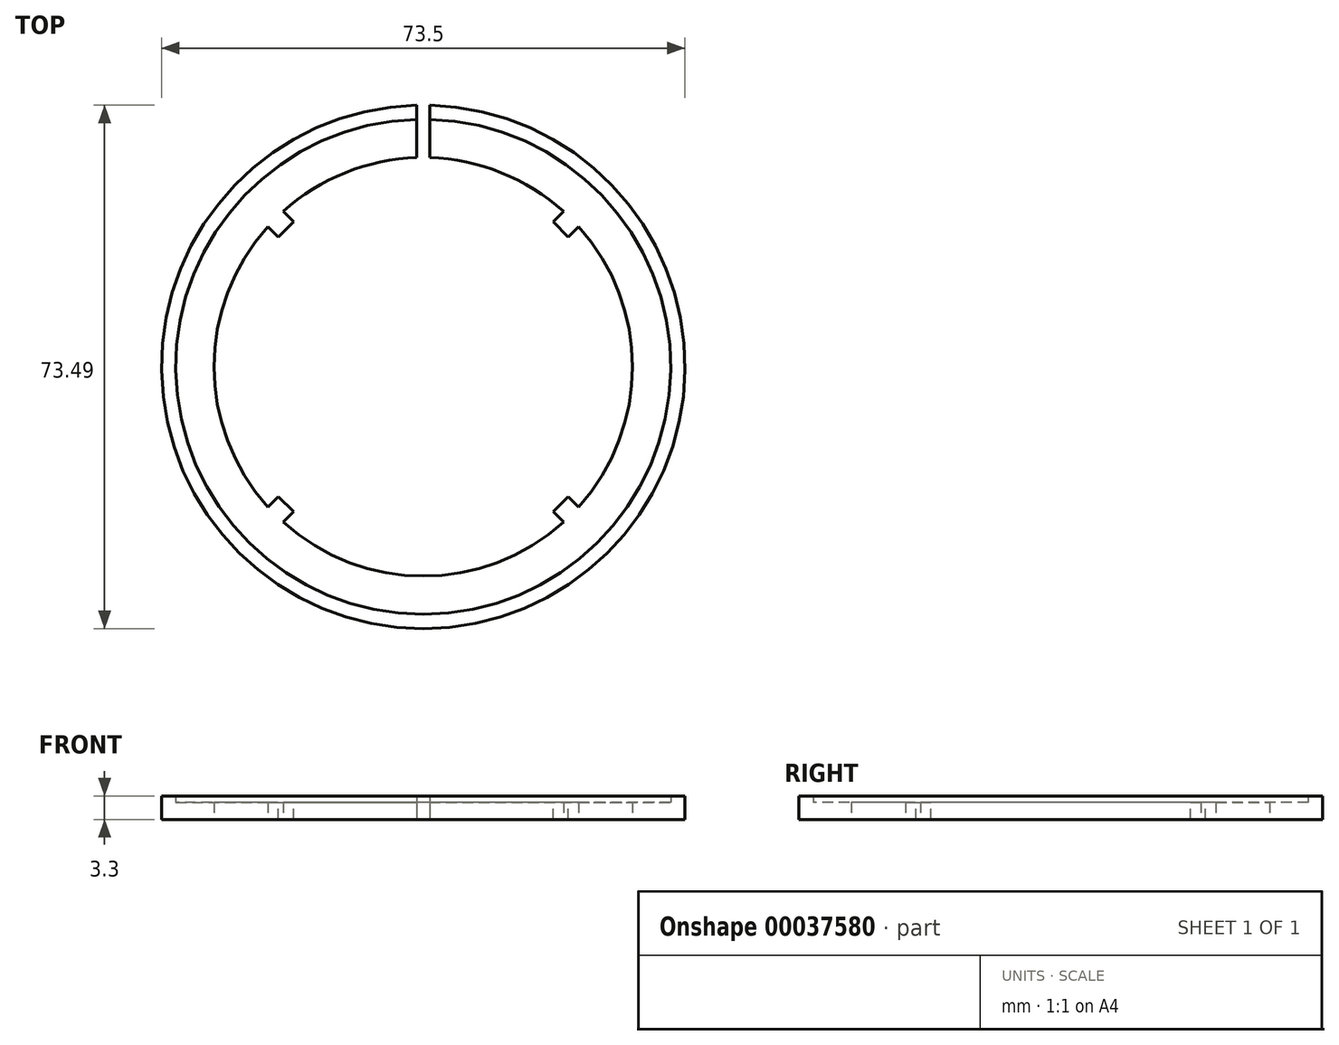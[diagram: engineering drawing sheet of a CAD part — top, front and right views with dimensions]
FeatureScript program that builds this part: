
annotation { "Feature Type Name" : "Feature", "Feature Type Description" : "" }
export const myFeature = defineFeature(function(context is Context, id is Id, definition is map)
    precondition{}
    {
        {
            var Q0;
            Q0=qCreatedBy(makeId("Right.planeOp"),FACE);
            var sketch = newSketch(context, id + "F0", { "sketchPlane" : qUnion([Q0])});
            skLineSegment(sketch, "E0", {"start": v(29.38, 0) * mm, "end": v(36.75, 0) * mm});
            skLineSegment(sketch, "E1", {"start": v(34.75, 2.4) * mm, "end": v(29.38, 2.4) * mm});
            skLineSegment(sketch, "E2", {"start": v(29.38, 2.4) * mm, "end": v(29.38, 0) * mm});
            skLineSegment(sketch, "E3", {"start": v(0, 0) * mm, "end": v(0, 55.42) * mm, "construction": true});
            skLineSegment(sketch, "E4", {"start": v(34.75, 2.4) * mm, "end": v(34.75, 3.3) * mm});
            skLineSegment(sketch, "E5", {"start": v(34.75, 3.3) * mm, "end": v(36.75, 3.3) * mm});
            skLineSegment(sketch, "E6", {"start": v(36.75, 3.3) * mm, "end": v(36.75, 0) * mm});
            skSolve(sketch);
        }
        {
            var Q0;
            Q0=makeQuery(id+"F0.imprint","IMPRINT",FACE,{"disambiguationData":[TD([[makeQuery(id+"F0.imprint","IMPRINT",EDGE,{"derivedFrom":sQuery(id+"F0.wireOp",EDGE,"E0")}),1.0]])]});
            var Q1;
            Q1=sQuery(id+"F0.wireOp",EDGE,"E3");
            revolve(context, id + "F1", {"entities" : qUnion([Q0]), "axis" : qUnion([Q1]), "revolveType" : RevolveType.FULL});
        }
        {
            var Q0;
            Q0=qCreatedBy(makeId("Top.planeOp"),FACE);
            var sketch = newSketch(context, id + "F2", { "sketchPlane" : qUnion([Q0])});
            skLineSegment(sketch, "E7.bottom", {"start": v(-0.9, 29.36) * mm, "end": v(0.9, 29.36) * mm});
            skLineSegment(sketch, "E7.top", {"start": v(-0.9, 36.75) * mm, "end": v(0.9, 36.75) * mm});
            skLineSegment(sketch, "E7.left", {"start": v(-0.9, 29.36) * mm, "end": v(-0.9, 36.75) * mm});
            skLineSegment(sketch, "E7.right", {"start": v(0.9, 29.36) * mm, "end": v(0.9, 36.75) * mm});
            skLineSegment(sketch, "E8", {"start": v(0, 0) * mm, "end": v(0, 36.75) * mm, "construction": true});
            skSolve(sketch);
        }
        {
            var Q0;
            {var subQ5=sQuery(id+"F2.wireOp",EDGE,"E7.bottom");Q0=makeQuery(id+"F2.imprint","IMPRINT",FACE,{"disambiguationData":[TD([[makeQuery(id+"F2.imprint","IMPRINT",EDGE,{"derivedFrom":subQ5}),1.0]])]});}
            var Q1;
            {var subQ0=sQuery(id+"F2.wireOp",EDGE,"E7.top");var subQ3=sQuery(id+"F2.wireOp",EDGE,"E7.left");var subQ4=makeQuery(id+"F2.imprint","INTERSECT",VERTEX,{"derivedFrom":[subQ3,subQ0]});Q1=makeQuery(id+"F2.imprint","IMPRINT",FACE,{"disambiguationData":[TD([[makeQuery(id+"F2.imprint","IMPRINT",EDGE,{"disambiguationData":[TD([[subQ4,1.0]])],"derivedFrom":subQ3}),-1.0]])]});}
            extrude(context, id + "F3", {"entities" : qUnion([Q0, Q1]), "operationType" : NewBodyOperationType.REMOVE, "endBound" : BoundingType.THROUGH_ALL, "depth" : 25 * mm});
        }
        {
            var Q0;
            Q0=makeQuery(id+"F1.opRevolve","SWEPT_FACE",FACE,{"disambiguationData":[OSD([sQuery(id+"F0.wireOp",EDGE,"E1")])]});
            var sketch = newSketch(context, id + "F4", { "sketchPlane" : qUnion([Q0])});
            skLineSegment(sketch, "E9.bottom", {"start": v(-19.71, 21.83) * mm, "end": v(-18.23, 20.35) * mm});
            skLineSegment(sketch, "E9.top", {"start": v(-21.83, 19.71) * mm, "end": v(-20.35, 18.23) * mm});
            skLineSegment(sketch, "E9.left", {"start": v(-19.71, 21.83) * mm, "end": v(-21.83, 19.71) * mm});
            skLineSegment(sketch, "E9.right", {"start": v(-18.23, 20.35) * mm, "end": v(-20.35, 18.23) * mm});
            skLineSegment(sketch, "E10", {"start": v(0, 0) * mm, "end": v(-20.77, 20.77) * mm, "construction": true});
            skPoint(sketch, "E11.center", {"position": v(0, 0) * mm});
            skSolve(sketch);
        }
        {
            var Q0;
            Q0=qSketchRegion(id+"F4",true);
            var Q1;
            {var subQ0=sQuery(id+"F2.wireOp",EDGE,"E7.top");var subQ1=sQuery(id+"F2.wireOp",EDGE,"cfe71888-e1f7-477f-a460-f0394f8c43ce.top");Q1=makeQuery(id+"FsA7NhVv1gf3l2V_1.boolean.opBoolean","MERGE",FACE,{"derivedFrom":[makeQuery(id+"F1.opRevolve","SWEPT_FACE",FACE,{"disambiguationData":[OSD([sQuery(id+"F0.wireOp",EDGE,"E0")])]}),makeQuery(id+"FsA7NhVv1gf3l2V_1.opExtrude","CAP_FACE",FACE,{"disambiguationData":[OSD([sQuery(id+"F2.wireOp",EDGE,"E7.left"),subQ0,subQ1,sQuery(id+"F2.wireOp",EDGE,"cfe71888-e1f7-477f-a460-f0394f8c43ce.left")])],"isStart":true}),makeQuery(id+"FsA7NhVv1gf3l2V_1.opExtrude","CAP_FACE",FACE,{"disambiguationData":[OSD([sQuery(id+"F2.wireOp",EDGE,"E7.right"),subQ0,subQ1,sQuery(id+"F2.wireOp",EDGE,"cfe71888-e1f7-477f-a460-f0394f8c43ce.right")])],"isStart":true})]});}
            extrude(context, id + "F5", {"entities" : qUnion([Q0]), "endBound" : BoundingType.UP_TO_SURFACE, "oppositeDirection" : true, "endBoundEntityFace" : qUnion([Q1]), "depth" : 25 * mm});
        }
        {
            var Q0;
            Q0=makeQuery(id+"F5.opExtrude","SWEPT_BODY",BODY,{"disambiguationData":[OSD([sQuery(id+"F4.wireOp",EDGE,"E9.bottom"),sQuery(id+"F4.wireOp",EDGE,"E9.top"),sQuery(id+"F4.wireOp",EDGE,"E9.left"),sQuery(id+"F4.wireOp",EDGE,"E9.right")])]});
            var Q1;
            Q1=makeQuery(id+"F1.opRevolve","SWEPT_FACE",FACE,{"disambiguationData":[OSD([sQuery(id+"F0.wireOp",EDGE,"E2")])]});
            circularPattern(context, id + "F6", {"operationType" : NewBodyOperationType.ADD, "entities" : qUnion([Q0]), "axis" : qUnion([Q1]), "angle" : 90 * degree, "instanceCount" : 4});
        }
    });
